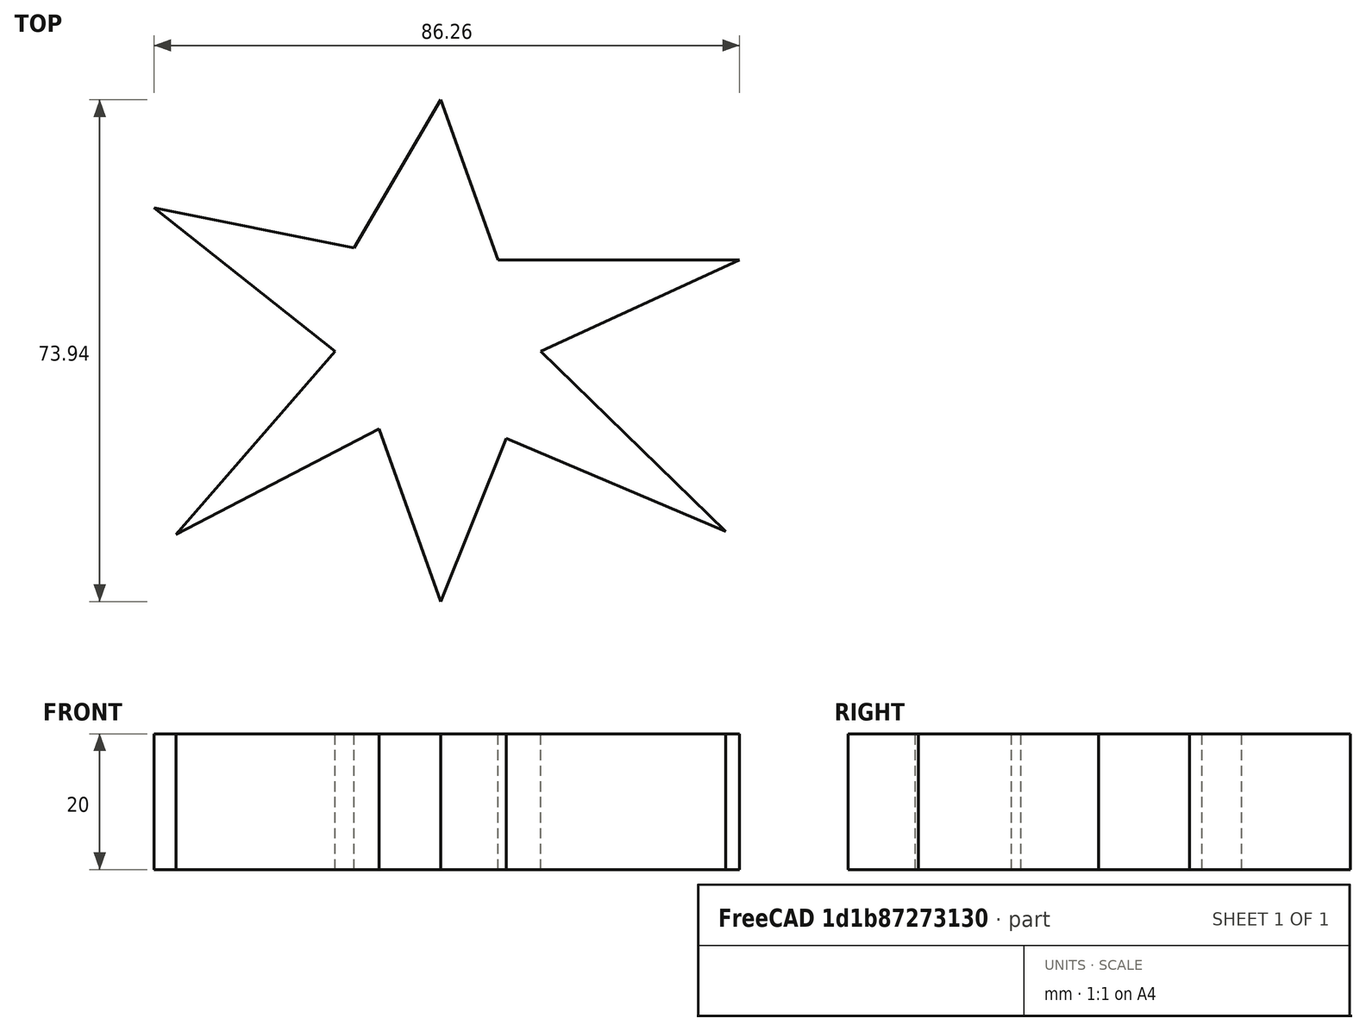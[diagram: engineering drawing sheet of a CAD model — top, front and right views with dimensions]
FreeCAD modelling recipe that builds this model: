
FCSTD DOCUMENT  (FreeCAD 0.21R33694 (Git))
Label: OJT1_T16P01_extrusio_estrella
License: All rights reserved
LicenseURL: https://en.wikipedia.org/wiki/All_rights_reserved
objects: Sketcher::SketchObject×1, PartDesign::Pad×1, PartDesign::Body×1
note: 4 computed .brp shape members not serialized (recipe doc carries the construction recipe); baked Part::Feature solids carry a one-line shape summary decoded from their .brp

FEATURE [Sketcher::SketchObject] Sketch  label="esboç-estrella"
  FullyConstrained = false
  MapMode = 5
  Support = -> [XY_Plane]
  sketch-geometry (12):
    g0: LineSegment StartX=1.8e-15 StartY=37.0707 StartZ=0 EndX=8.48485 EndY=13.4343 EndZ=0
    g1: LineSegment StartX=8.48485 StartY=13.4343 StartZ=0 EndX=44.0404 EndY=13.4343 EndZ=0
    g2: LineSegment StartX=44.0404 StartY=13.4343 StartZ=0 EndX=14.7475 EndY=0 EndZ=0
    g3: LineSegment StartX=14.7475 StartY=0 StartZ=0 EndX=42.0202 EndY=-26.5657 EndZ=0
    g4: LineSegment StartX=42.0202 StartY=-26.5657 StartZ=0 EndX=9.69697 EndY=-12.8283 EndZ=0
    g5: LineSegment StartX=9.69697 StartY=-12.8283 StartZ=0 EndX=0 EndY=-36.8687 EndZ=0
    g6: LineSegment StartX=0 StartY=-36.8687 StartZ=0 EndX=-9.09091 EndY=-11.4141 EndZ=0
    g7: LineSegment StartX=-9.09091 StartY=-11.4141 StartZ=0 EndX=-38.9899 EndY=-26.9697 EndZ=0
    g8: LineSegment StartX=-38.9899 StartY=-26.9697 StartZ=0 EndX=-15.5556 EndY=0 EndZ=0
    g9: LineSegment StartX=-15.5556 StartY=0 StartZ=0 EndX=-42.2222 EndY=21.1111 EndZ=0
    g10: LineSegment StartX=-42.2222 StartY=21.1111 StartZ=0 EndX=-12.7273 EndY=15.2525 EndZ=0
    g11: LineSegment StartX=-12.7273 StartY=15.2525 StartZ=0 EndX=1.8e-15 EndY=37.0707 EndZ=0
  constraints (17):
    c: PointOnObject(g0,g-2)
    c: Coincident(g0,g1)
    c: Horizontal(g1)
    c: Coincident(g1,g2)
    c: PointOnObject(g2,g-1)
    c: Coincident(g2,g3)
    c: Coincident(g3,g4)
    c: Coincident(g4,g5)
    c: PointOnObject(g5,g-2)
    c: Coincident(g5,g6)
    c: Coincident(g6,g7)
    c: Coincident(g7,g8)
    c: PointOnObject(g8,g-1)
    c: Coincident(g8,g9)
    c: Coincident(g9,g10)
    c: Coincident(g10,g11)
    c: Coincident(g11,g0)
FEATURE [PartDesign::Pad] Pad  label="ESTRELLA"
  Direction = (0,0,1)
  Length = 20
  Length2 = 10
  Profile = -> Sketch
  ReferenceAxis = -> Sketch [N_Axis]
  Type = 0
FEATURE [PartDesign::Body] Body
  Group = -> [Sketch,Pad]
  Origin = -> Origin
  Tip = -> Pad
